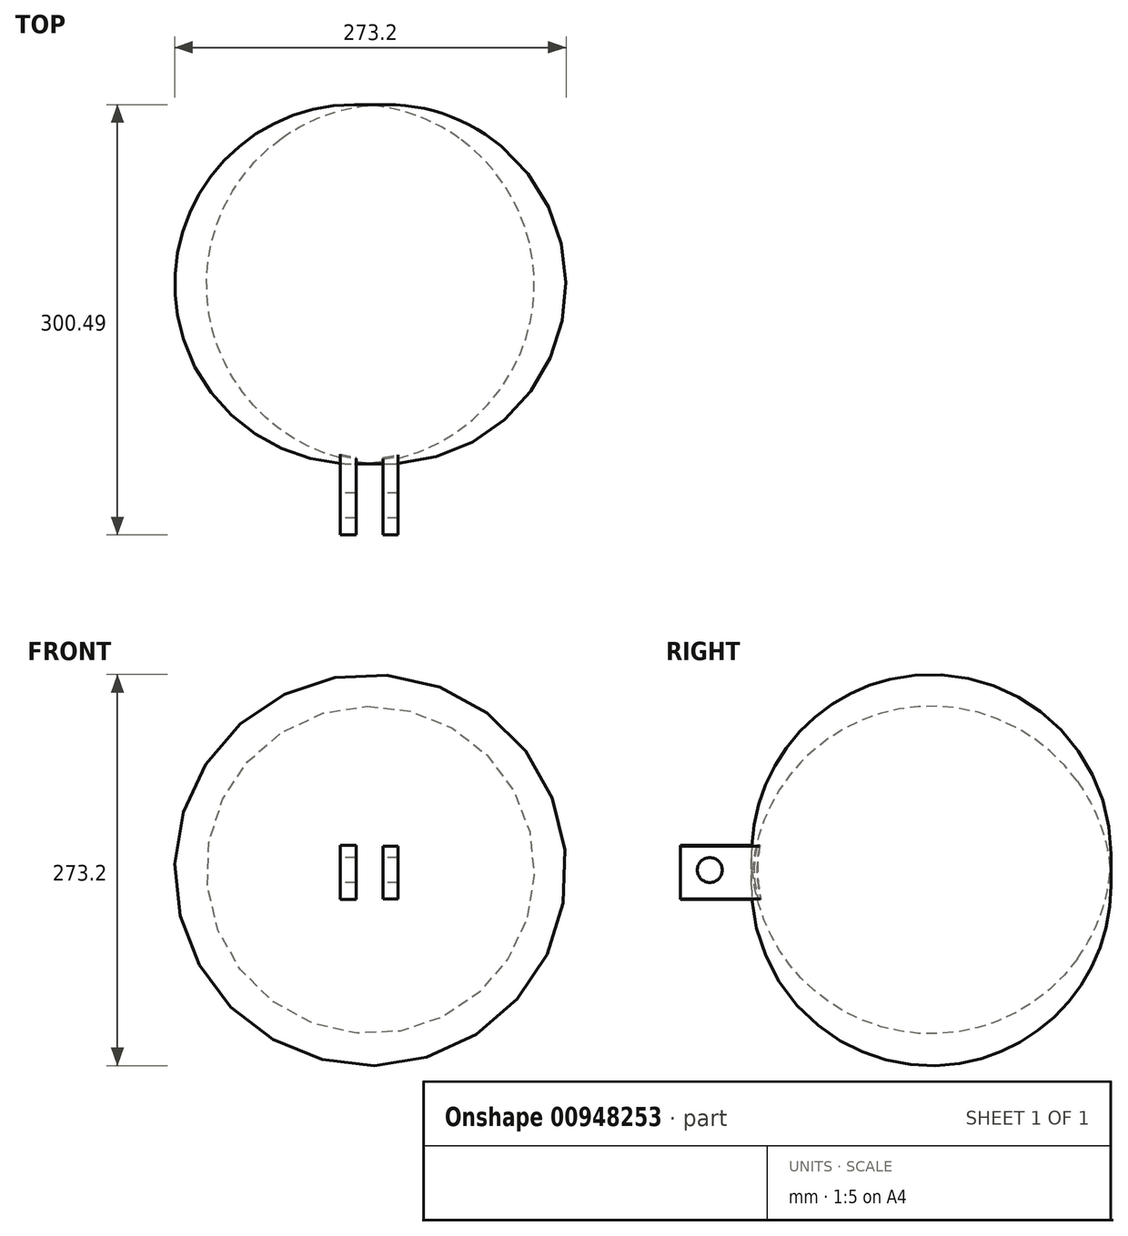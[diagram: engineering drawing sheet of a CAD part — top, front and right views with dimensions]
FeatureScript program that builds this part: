
annotation { "Feature Type Name" : "Feature", "Feature Type Description" : "" }
export const myFeature = defineFeature(function(context is Context, id is Id, definition is map)
    precondition{}
    {
        {
            var Q0;
            Q0=qCreatedBy(makeId("Top.planeOp"),FACE);
            var sketch = newSketch(context, id + "F0", { "sketchPlane" : qUnion([Q0])});
            skArc(sketch, "E0", {"start": v(0, 0) * mm, "mid": v(114.39, 125) * mm, "end": v(0, 250) * mm});
            skLineSegment(sketch, "E1", {"start": v(0, 250) * mm, "end": v(0, 0) * mm});
            skSolve(sketch);
        }
        {
            var Q0;
            Q0=makeQuery(id+"F0.imprint","IMPRINT",FACE,{"disambiguationData":[TD([[makeQuery(id+"F0.imprint","IMPRINT",EDGE,{"derivedFrom":sQuery(id+"F0.wireOp",EDGE,"E0")}),1.0]])]});
            var Q1;
            Q1=sQuery(id+"F0.wireOp",EDGE,"E1");
            revolve(context, id + "F1", {"surfaceOperationType" : NewSurfaceOperationType.NEW, "entities" : qUnion([Q0]), "axis" : qUnion([Q1]), "revolveType" : RevolveType.FULL});
        }
        {
            var Q0;
            Q0=qCreatedBy(makeId("Front.planeOp"),FACE);
            cPlane(context, id + "F2", {"entities" : qUnion([Q0]), "cplaneType" : CPlaneType.OFFSET, "offset" : 25 * mm, "oppositeDirection" : true, "width" : 150 * mm, "height" : 150 * mm});
        }
        {
            var Q0;
            Q0=qCreatedBy(id+"F2.planeOp",FACE);
            var sketch = newSketch(context, id + "F3", { "sketchPlane" : qUnion([Q0])});
            skLineSegment(sketch, "E2.bottom", {"start": v(-20.99, 17.24) * mm, "end": v(-10.07, 17.24) * mm});
            skLineSegment(sketch, "E2.top", {"start": v(-20.99, -20.4) * mm, "end": v(-10.07, -20.4) * mm});
            skLineSegment(sketch, "E2.left", {"start": v(-20.99, 17.24) * mm, "end": v(-20.99, -20.4) * mm});
            skLineSegment(sketch, "E2.right", {"start": v(-10.07, 17.24) * mm, "end": v(-10.07, -20.4) * mm});
            skLineSegment(sketch, "E3.bottom", {"start": v(8.94, 16.75) * mm, "end": v(19.37, 16.75) * mm});
            skLineSegment(sketch, "E3.top", {"start": v(8.94, -20.31) * mm, "end": v(19.37, -20.31) * mm});
            skLineSegment(sketch, "E3.left", {"start": v(8.94, 16.75) * mm, "end": v(8.94, -20.31) * mm});
            skLineSegment(sketch, "E3.right", {"start": v(19.37, 16.75) * mm, "end": v(19.37, -20.31) * mm});
            skSolve(sketch);
        }
        {
            var Q0;
            Q0=makeQuery(id+"F3.imprint","IMPRINT",FACE,{"disambiguationData":[TD([[makeQuery(id+"F3.imprint","IMPRINT",EDGE,{"derivedFrom":sQuery(id+"F3.wireOp",EDGE,"E2.bottom")}),-1.0]])]});
            var Q1;
            Q1=makeQuery(id+"F3.imprint","IMPRINT",FACE,{"disambiguationData":[TD([[makeQuery(id+"F3.imprint","IMPRINT",EDGE,{"derivedFrom":sQuery(id+"F3.wireOp",EDGE,"E3.bottom")}),-1.0]])]});
            extrude(context, id + "F4", {"entities" : qUnion([Q0, Q1]), "operationType" : NewBodyOperationType.ADD, "depth" : 75 * mm, "offsetDistance" : 25 * mm});
        }
        {
            var Q0;
            Q0=makeQuery(id+"F4.opExtrude","SWEPT_FACE",FACE,{"disambiguationData":[OSD([sQuery(id+"F3.wireOp",EDGE,"E2.left")])]});
            var sketch = newSketch(context, id + "F5", { "sketchPlane" : qUnion([Q0])});
            skCircle(sketch, "E4", {"center": v(29.62, 0) * mm, "radius": 8.7 * mm});
            skSolve(sketch);
        }
        {
            var Q0;
            Q0=makeQuery(id+"F5.imprint","IMPRINT",FACE,{"disambiguationData":[TD([[makeQuery(id+"F5.imprint","IMPRINT",EDGE,{"derivedFrom":sQuery(id+"F5.wireOp",EDGE,"E4")}),1.0]])]});
            extrude(context, id + "F6", {"entities" : qUnion([Q0]), "operationType" : NewBodyOperationType.REMOVE, "endBound" : BoundingType.THROUGH_ALL, "oppositeDirection" : true, "depth" : 25 * mm, "offsetDistance" : 25 * mm});
        }
    });
